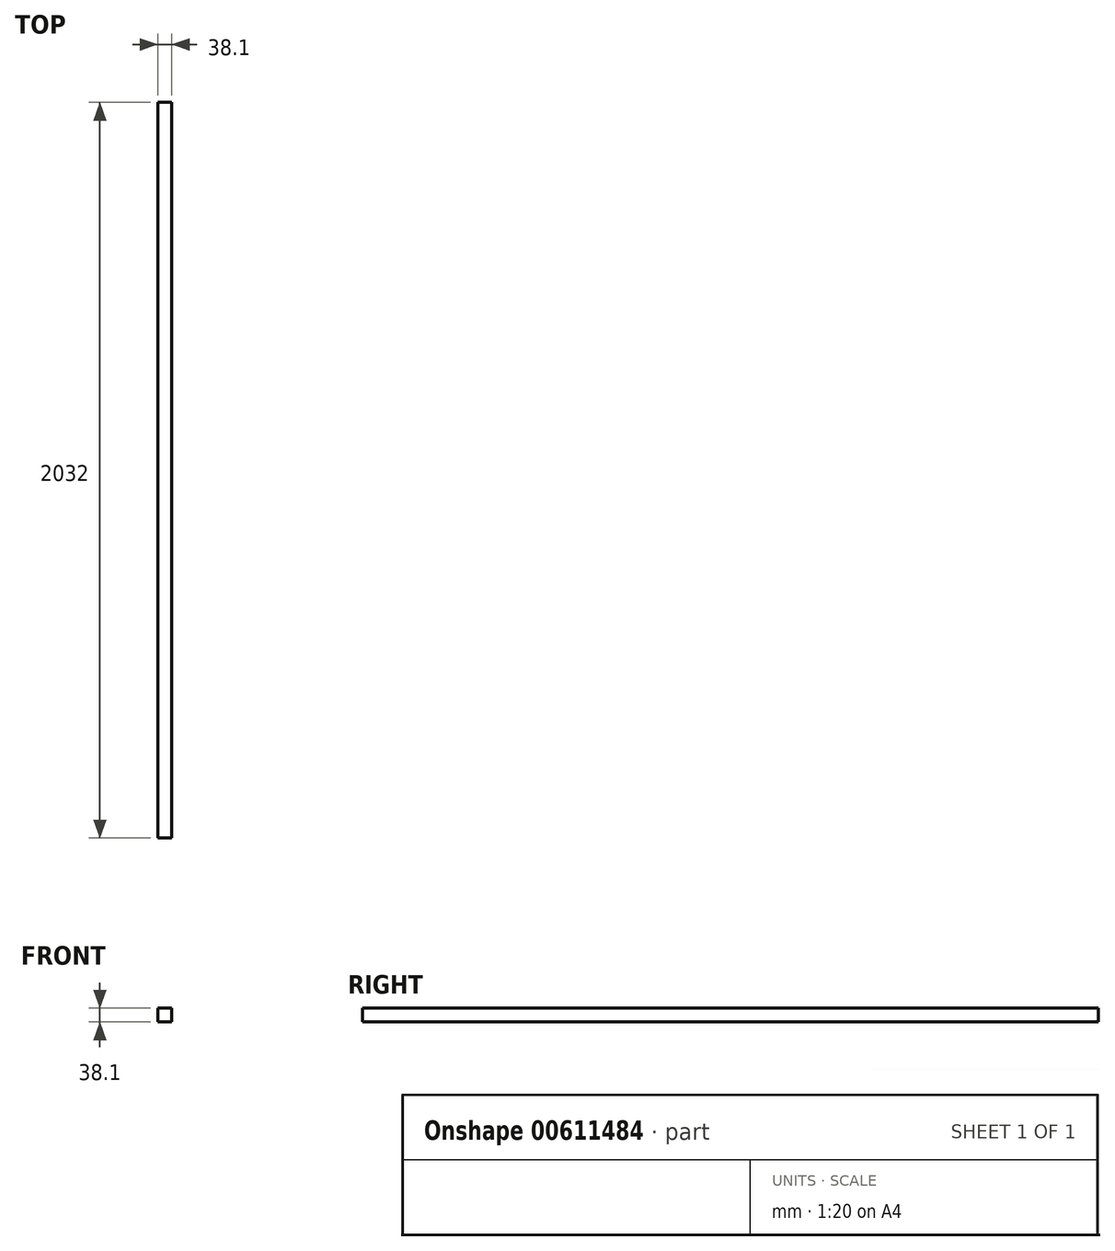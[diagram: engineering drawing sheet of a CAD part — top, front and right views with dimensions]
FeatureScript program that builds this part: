
annotation { "Feature Type Name" : "Feature", "Feature Type Description" : "" }
export const myFeature = defineFeature(function(context is Context, id is Id, definition is map)
    precondition{}
    {
        {
            var Q0;
            Q0=qCreatedBy(makeId("Front.planeOp"),FACE);
            var sketch = newSketch(context, id + "F0", { "sketchPlane" : qUnion([Q0])});
            skLineSegment(sketch, "E0.bottom", {"start": v(0, 0) * mm, "end": v(38.1, 0) * mm});
            skLineSegment(sketch, "E0.top", {"start": v(0, -38.1) * mm, "end": v(38.1, -38.1) * mm});
            skLineSegment(sketch, "E0.left", {"start": v(0, 0) * mm, "end": v(0, -38.1) * mm});
            skLineSegment(sketch, "E0.right", {"start": v(38.1, 0) * mm, "end": v(38.1, -38.1) * mm});
            skSolve(sketch);
        }
        {
            var Q0;
            Q0 = qSketchRegion(id + "F0", true);
            extrude(context, id + "F1", {"entities" : qUnion([Q0]), "depth" : 2032 * mm, "offsetDistance" : 25.4 * mm});
        }
    });
